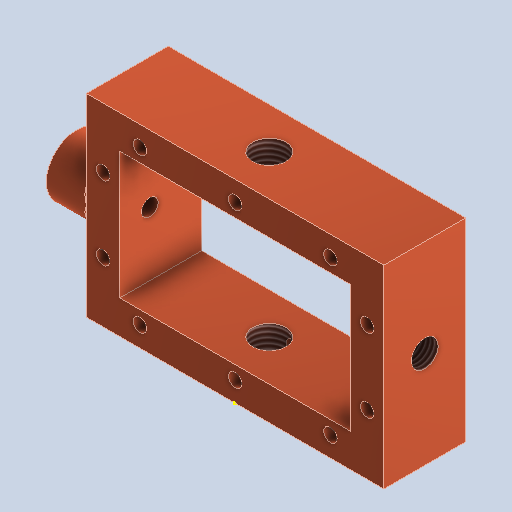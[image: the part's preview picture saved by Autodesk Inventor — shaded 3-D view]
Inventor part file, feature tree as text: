
AUTODESK INVENTOR PART (.ipt)
format: ipt  version: 2025.1 (Build 291241000, 241)  size: 226,816 bytes
history: native  units: mm
features: sketch x9, other x3, plane x2
ambient origin geometry x8: Origin, YZ Plane, XZ Plane, XY Plane, X Axis, Y Axis, Z Axis, Center Point
bodies: Volumenkörper1 (feature_tree)
feature tree (14):
  other  "1152_body.ipt"
  other  "Volumenkörper1::1152_body.ipt"
  other  "TaggingFeature1"
  sketch  "Skizze1"  dims[d0=10.0mm]
  sketch  "Skizze2"
  sketch  "Skizze3"
  sketch  "Skizze4"
  sketch  "Skizze5"
  sketch  "Skizze6"
  sketch  "Skizze7"
  sketch  "Skizze9"
  sketch  "Skizze10"
  plane  "Arbeitsebene1"
  plane  "Arbeitsebene3"
